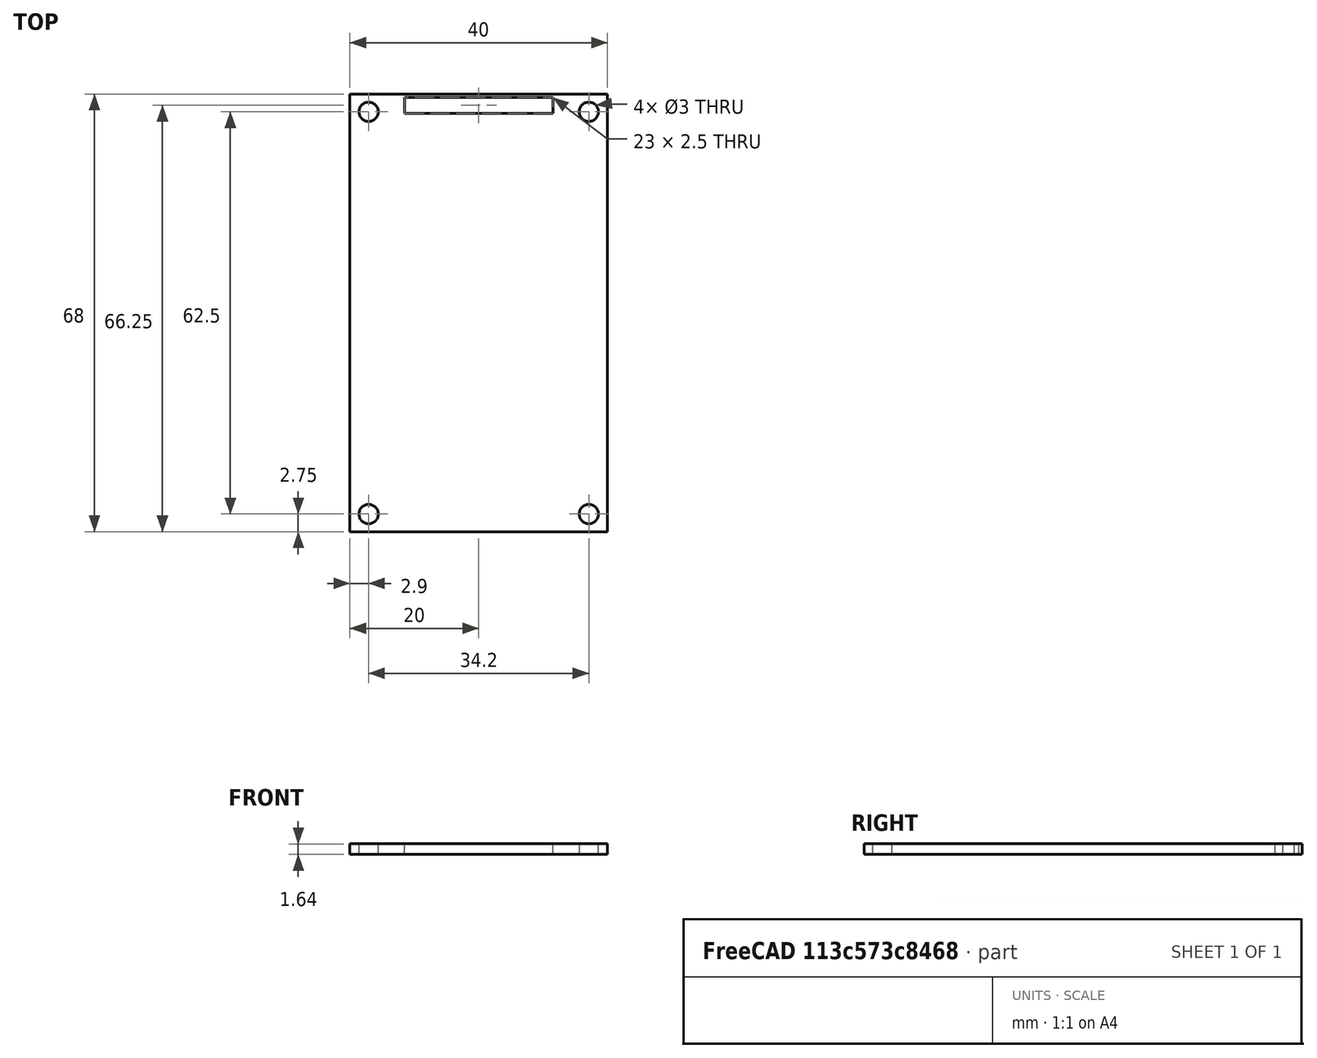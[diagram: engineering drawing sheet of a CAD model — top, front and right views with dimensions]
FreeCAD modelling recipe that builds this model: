
FCSTD DOCUMENT  (FreeCAD 0.15R4671 (Git))
Label: tft
License: CreativeCommons Attribution
LicenseURL: http://creativecommons.org/licenses/by/4.0/
objects: Sketcher::SketchObject×1, PartDesign::Pad×1
note: 3 computed .brp shape members not serialized (recipe doc carries the construction recipe); baked Part::Feature solids carry a one-line shape summary decoded from their .brp

FEATURE [Sketcher::SketchObject] Sketch
  sketch-geometry (18):
    g0: Circle CenterX=-17.1 CenterY=31.25 CenterZ=0 NormalX=0 NormalY=0 NormalZ=1 Radius=1.5
    g1: Circle CenterX=17.1 CenterY=31.25 CenterZ=0 NormalX=0 NormalY=0 NormalZ=1 Radius=1.5
    g2: Circle CenterX=-17.1 CenterY=-31.25 CenterZ=0 NormalX=0 NormalY=0 NormalZ=1 Radius=1.5
    g3: Circle CenterX=17.1 CenterY=-31.25 CenterZ=0 NormalX=0 NormalY=0 NormalZ=1 Radius=1.5
    g4: LineSegment StartX=-20 StartY=34 StartZ=0 EndX=20 EndY=34 EndZ=0
    g5: LineSegment StartX=20 StartY=34 StartZ=0 EndX=20 EndY=-34 EndZ=0
    g6: LineSegment StartX=20 StartY=-34 StartZ=0 EndX=-20 EndY=-34 EndZ=0
    g7: LineSegment StartX=-20 StartY=-34 StartZ=0 EndX=-20 EndY=34 EndZ=0
    g8: GeomPoint [constr] X=-17.1 Y=32.75 Z=0
    g9: GeomPoint [constr] X=-18.6 Y=31.25 Z=0
    g10: LineSegment [constr] StartX=-17.1 StartY=32.75 StartZ=0 EndX=-17.1 EndY=34 EndZ=0
    g11: LineSegment [constr] StartX=-18.6 StartY=31.25 StartZ=0 EndX=-20 EndY=31.25 EndZ=0
    g12: LineSegment StartX=-11.5 StartY=33.5 StartZ=0 EndX=11.5 EndY=33.5 EndZ=0
    g13: LineSegment StartX=11.5 StartY=33.5 StartZ=0 EndX=11.5 EndY=31 EndZ=0
    g14: LineSegment StartX=11.5 StartY=31 StartZ=0 EndX=-11.5 EndY=31 EndZ=0
    g15: LineSegment StartX=-11.5 StartY=31 StartZ=0 EndX=-11.5 EndY=33.5 EndZ=0
    g16: LineSegment [constr] StartX=-18.6 StartY=31.25 StartZ=0 EndX=-17.1 EndY=31.25 EndZ=0
    g17: LineSegment [constr] StartX=-17.1 StartY=31.25 StartZ=0 EndX=-17.1 EndY=32.75 EndZ=0
  constraints (46):
    c: Equal(g0,g1)
    c: Equal(g1,g3)
    c: Equal(g3,g2)
    c: Symmetric(g0,g1,g-2)
    c: Symmetric(g2,g0,g-1)
    c: Symmetric(g3,g1,g-1)
    c: Coincident(g4,g5)
    c: Coincident(g5,g6)
    c: Coincident(g6,g7)
    c: Coincident(g7,g4)
    c: Horizontal(g6)
    c: Vertical(g5)
    c: Vertical(g7)
    c: Symmetric(g4,g5,g-1)
    c: Symmetric(g4,g4,g-2)
    c: DistanceX(g4,g4) = 40
    c: DistanceY(g4,g6) = -68
    c: PointOnObject(g9,g0)
    c: Coincident(g10,g8)
    c: PointOnObject(g10,g4)
    c: Coincident(g11,g9)
    c: PointOnObject(g11,g7)
    c: Horizontal(g11)
    c: Vertical(g10)
    c: DistanceY(g10,g8) = -1.25
    c: DistanceX(g9,g11) = -1.4
    c: Coincident(g12,g13)
    c: Coincident(g13,g14)
    c: Coincident(g14,g15)
    c: Coincident(g15,g12)
    c: Horizontal(g12)
    c: Horizontal(g14)
    c: Vertical(g13)
    c: Vertical(g15)
    c: Distance(g14,g4) = 3
    c: DistanceY(g12,g13) = -2.5
    c: DistanceX(g13,g14) = -23
    c: DistanceX(g4,g13) = 31.5
    c: Radius(g1) = 1.5
    c: Coincident(g16,g9)
    c: Coincident(g16,g0)
    c: Horizontal(g16)
    c: Vertical(g17)
    c: PointOnObject(g17,g0)
    c: Coincident(g17,g8)
    c: Coincident(g0,g17)
FEATURE [PartDesign::Pad] Pad
  Length = 1.65
  Length2 = 100
  Midplane = true
  Sketch = -> Sketch
  Type = 0
